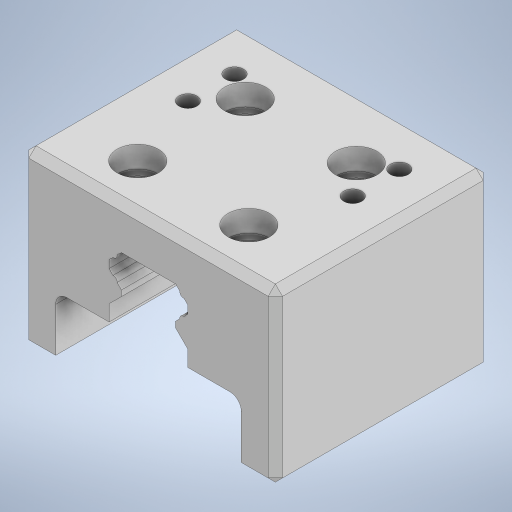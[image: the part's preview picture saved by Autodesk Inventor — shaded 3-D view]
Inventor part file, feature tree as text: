
AUTODESK INVENTOR PART (.ipt)
format: ipt  version: 2023 (Build 270158000, 158)  size: 397,824 bytes
history: native  units: in
note: dims shown in document units (in); Inventor stores cm internally (conversion verified against a paired STEP export)
features: extrude x7, sketch x3, thicken_offset x1, chamfer x1
ambient origin geometry x8: Origin, YZ Plane, XZ Plane, XY Plane, X Axis, Y Axis, Z Axis, Center Point
bodies: Solid1 (feature_tree)
feature tree (12):
  extrude  "Extrusion1"  Depth=2.3622in
  extrude  "Extrusion2"  Depth=0.0197in
  extrude  "Extrusion3"  Depth=0.0787in
  extrude  "Extrusion4"  Depth=0.1969in
  extrude  "Extrusion5"  Depth=0.0787in
  extrude  "Extrusion6"  Depth=0.0787in
  extrude  "Extrusion9"  Depth=2.7874in
  thicken_offset  "Thicken1"
  chamfer  "Chamfer1"  Distance=2.3622in
  sketch  "Sketch4"  dims[d0=0.9843in d1=2.3622in]
  sketch  "Sketch5"  dims[d2=0.0197in d3=0.0197in]
  sketch  "Sketch8"  dims[d4=0.0197in d5=0.0197in d6=0.1969in d7=1.811in d8=0.5118in d9=2.7874in d10=2.3622in d11=1.3937in d12=0.0in d13=1.3937in d14=0.0in d15=0.3937in d16=0.1969in d17=0.0in d18=0.0in d19=0.3937in d20=1.1969in d21=0.0in d22=0.0in d27=0.3937in d28=0.0in d29=0.2687in d31=1.4375in d32=0.0in d34=0.4528in d35=0.2362in d36=0.0in d50=1.3937in d51=0.0394in d52=0.1181in d53=135.0deg d54=0.0787in d55=0.1358in d56=0.689in d57=0.2819in d58=0.0935in d59=0.0525in d60=0.0953in d61=0.3937in d63=0.3937in d64=0.0in d66=0.0394in d67=0.125in d68=0.374in d69=0.689in d70=90.0deg d71=90.0deg d72=0.7874in d73=0.0394in d74=0.689in d78=1.1811in d79=1.2205in d80=0.689in d81=0.0787in d82=0.0787in d83=45.0deg d84=0.0787in]
